# Revit family: Pluraluce M LED 1-s Sentr (høyre_veggmontasje)
name_source: partatom
category: Lighting Fixtures
revit_build: Autodesk Revit 2013 (Build: 20130531_2115(x64)
units: mm (PartAtom-declared; Revit-internal decimal feet)

## types (2) — shared parameters
Apparent Load = 17 VA
Body Material and Colour = Default
Color Filter = 16777215
Dimming Lamp Color Temperature Shift = <None>
Emit Shape Visible in Rendering = No
Lamp = 1
Number of Poles = 1
Photometric Web File = 20x42A12.ies
Tilt Angle = 90.00°
Voltage = 230 V
Wattage Comments = 17 W
Width = 10 mm  [stored 0.0328084 ft]

## per-type parameters (varying)
| type | 20m | 30m | Emit from Rectangle Length | Emit from Rectangle Width | Height | Height 1 | Length | Length 1 |
| 20m | Yes | No | 235 mm  [stored 0.770997 ft] | 135 mm  [stored 0.442913 ft] | 135 mm  [stored 0.442913 ft] | 105 mm  [stored 0.344488 ft] | 235 mm  [stored 0.770997 ft] | 205 mm  [stored 0.672572 ft] |
| 30m | No | Yes | 335 mm | 185 mm | 185 mm | 155 mm  [stored 0.50853 ft] | 335 mm | 305 mm |

note: [stored X ft] marks values corroborated as IEEE doubles in the binary element streams (Revit-internal decimal feet)

## geometry (parser evidence)
native form markers: Sweep x6
no freeform markers — native parametric forms only
